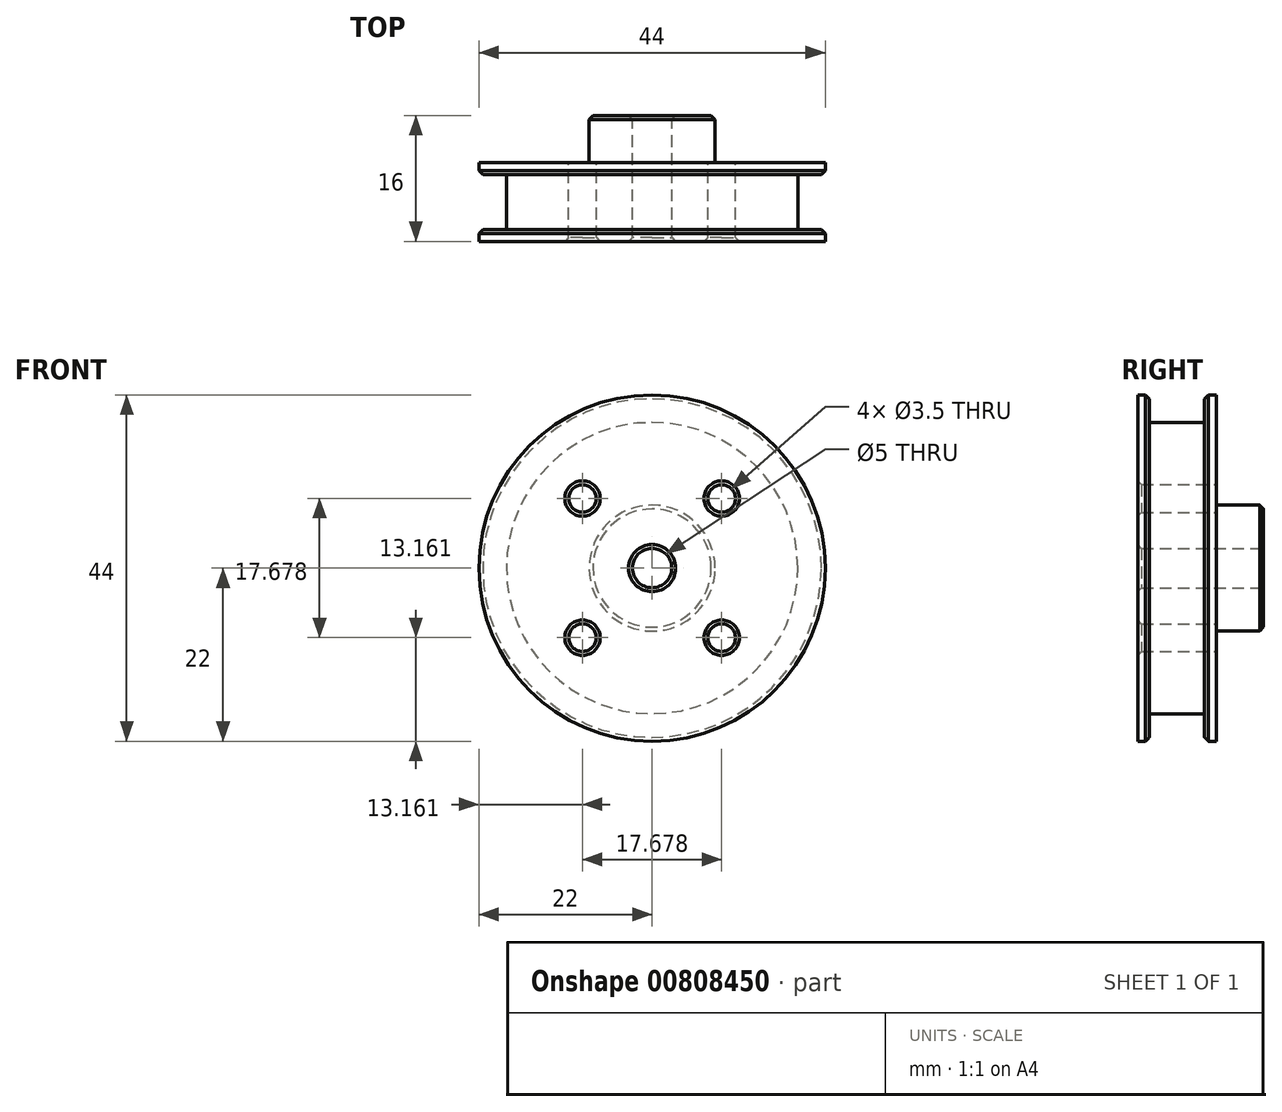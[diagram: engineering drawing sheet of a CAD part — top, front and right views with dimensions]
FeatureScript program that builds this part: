
annotation { "Feature Type Name" : "Feature", "Feature Type Description" : "" }
export const myFeature = defineFeature(function(context is Context, id is Id, definition is map)
    precondition{}
    {
        {
            var Q0;
            Q0=qCreatedBy(makeId("Front.planeOp"),FACE);
            var sketch = newSketch(context, id + "F0", { "sketchPlane" : qUnion([Q0])});
            skCircle(sketch, "E0", {"center": v(0, 0) * mm, "radius": 22 * mm});
            skSolve(sketch);
        }
        {
            var Q0;
            Q0=qSketchRegion(id+"F0",true);
            extrude(context, id + "F1", {"entities" : qUnion([Q0]), "depth" : 10 * mm, "offsetDistance" : 25 * mm, "symmetric" : true});
        }
        {
            var Q0;
            Q0=qCreatedBy(makeId("Front.planeOp"),FACE);
            var sketch = newSketch(context, id + "F2", { "sketchPlane" : qUnion([Q0])});
            skCircle(sketch, "E1", {"center": v(0, 0) * mm, "radius": 18.5 * mm});
            skCircle(sketch, "E2", {"center": v(0, 0) * mm, "radius": 30.43 * mm});
            skSolve(sketch);
        }
        {
            var Q0;
            Q0=qSketchRegion(id+"F2",true);
            extrude(context, id + "F3", {"entities" : qUnion([Q0]), "operationType" : NewBodyOperationType.REMOVE, "depth" : 7 * mm, "offsetDistance" : 25 * mm, "symmetric" : true});
        }
        {
            var Q0;
            Q0=makeQuery(id+"F1.opExtrude","CAP_FACE",FACE,{"disambiguationData":[OSD([sQuery(id+"F0.wireOp",EDGE,"E0")])],"isStart":true});
            var sketch = newSketch(context, id + "F4", { "sketchPlane" : qUnion([Q0])});
            skCircle(sketch, "E3", {"center": v(0, 0) * mm, "radius": 8 * mm});
            skSolve(sketch);
        }
        {
            var Q0;
            Q0=qSketchRegion(id+"F4",true);
            extrude(context, id + "F5", {"entities" : qUnion([Q0]), "operationType" : NewBodyOperationType.ADD, "depth" : 6 * mm, "offsetDistance" : 25 * mm});
        }
        {
            var Q0;
            Q0=makeQuery(id+"F5.opExtrude","CAP_FACE",FACE,{"disambiguationData":[OSD([sQuery(id+"F4.wireOp",EDGE,"E3")])],"isStart":false});
            var sketch = newSketch(context, id + "F6", { "sketchPlane" : qUnion([Q0])});
            skCircle(sketch, "E4", {"center": v(0, 0) * mm, "radius": 2.5 * mm});
            skSolve(sketch);
        }
        {
            var Q0;
            Q0=qSketchRegion(id+"F6",true);
            extrude(context, id + "F7", {"entities" : qUnion([Q0]), "operationType" : NewBodyOperationType.REMOVE, "endBound" : BoundingType.THROUGH_ALL, "oppositeDirection" : true, "depth" : 25 * mm, "offsetDistance" : 25 * mm});
        }
        {
            var Q0;
            Q0=makeQuery(id+"F5.opExtrude","CAP_FACE",FACE,{"disambiguationData":[OSD([sQuery(id+"F4.wireOp",EDGE,"E3")])],"isStart":false});
            var Q1;
            Q1=makeQuery(id+"F5.opExtrude","CAP_EDGE",EDGE,{"disambiguationData":[OSD([sQuery(id+"F4.wireOp",EDGE,"E3")])],"isStart":true});
            var Q2;
            Q2=makeQuery(id+"F3.boolean.opBoolean","INTERSECT",EDGE,{"derivedFrom":[makeQuery(id+"F1.opExtrude","SWEPT_FACE",FACE,{"disambiguationData":[OSD([sQuery(id+"F0.wireOp",EDGE,"E0")])]}),makeQuery(id+"F3.opExtrude","CAP_FACE",FACE,{"disambiguationData":[OSD([sQuery(id+"F2.wireOp",EDGE,"E1"),sQuery(id+"F2.wireOp",EDGE,"E2")])],"isStart":true})]});
            var Q3;
            Q3=makeQuery(id+"F3.boolean.opBoolean","INTERSECT",EDGE,{"derivedFrom":[makeQuery(id+"F1.opExtrude","SWEPT_FACE",FACE,{"disambiguationData":[OSD([sQuery(id+"F0.wireOp",EDGE,"E0")])]}),makeQuery(id+"F3.opExtrude","CAP_FACE",FACE,{"disambiguationData":[OSD([sQuery(id+"F2.wireOp",EDGE,"E1"),sQuery(id+"F2.wireOp",EDGE,"E2")])],"isStart":false})]});
            var Q4;
            Q4=makeQuery(id+"F7.boolean.opBoolean","INTERSECT",EDGE,{"derivedFrom":[makeQuery(id+"F1.opExtrude","CAP_FACE",FACE,{"disambiguationData":[OSD([sQuery(id+"F0.wireOp",EDGE,"E0")])],"isStart":false}),makeQuery(id+"F7.opExtrude","SWEPT_FACE",FACE,{"disambiguationData":[OSD([sQuery(id+"F6.wireOp",EDGE,"E4")])]})]});
            chamfer(context, id + "F8", {"entities" : qUnion([Q0, Q1, Q2, Q3, Q4]), "width" : 0.5 * mm, "tangentPropagation" : true});
        }
        {
            var Q0;
            Q0=makeQuery(id+"F1.opExtrude","CAP_FACE",FACE,{"disambiguationData":[OSD([sQuery(id+"F0.wireOp",EDGE,"E0")])],"isStart":true});
            var sketch = newSketch(context, id + "F9", { "sketchPlane" : qUnion([Q0])});
            skCircle(sketch, "E5", {"center": v(-8.84, 8.84) * mm, "radius": 1.75 * mm});
            skLineSegment(sketch, "E6", {"start": v(-22, 0) * mm, "end": v(0, 0) * mm, "construction": true});
            skLineSegment(sketch, "E7", {"start": v(0, 0) * mm, "end": v(-8.84, 8.84) * mm, "construction": true});
            skCircle(sketch, "E8.1.0", {"center": v(-8.84, -8.84) * mm, "radius": 1.75 * mm});
            skCircle(sketch, "E8.2.0", {"center": v(8.84, -8.84) * mm, "radius": 1.75 * mm});
            skCircle(sketch, "E8.3.0", {"center": v(8.84, 8.84) * mm, "radius": 1.75 * mm});
            skPoint(sketch, "E8.center", {"position": v(0, 0) * mm});
            skSolve(sketch);
        }
        {
            var Q0;
            Q0=qSketchRegion(id+"F9",true);
            extrude(context, id + "F10", {"entities" : qUnion([Q0]), "operationType" : NewBodyOperationType.REMOVE, "endBound" : BoundingType.THROUGH_ALL, "oppositeDirection" : true, "depth" : 25 * mm, "offsetDistance" : 25 * mm});
        }
        {
            var Q0;
            Q0=makeQuery(id+"F10.boolean.opBoolean","INTERSECT",EDGE,{"derivedFrom":[makeQuery(id+"F1.opExtrude","CAP_FACE",FACE,{"disambiguationData":[OSD([sQuery(id+"F0.wireOp",EDGE,"E0")])],"isStart":false}),makeQuery(id+"F10.opExtrude","SWEPT_FACE",FACE,{"disambiguationData":[OSD([sQuery(id+"F9.wireOp",EDGE,"E8.3.0")])]})]});
            var Q1;
            Q1=makeQuery(id+"F10.boolean.opBoolean","INTERSECT",EDGE,{"derivedFrom":[makeQuery(id+"F1.opExtrude","CAP_FACE",FACE,{"disambiguationData":[OSD([sQuery(id+"F0.wireOp",EDGE,"E0")])],"isStart":false}),makeQuery(id+"F10.opExtrude","SWEPT_FACE",FACE,{"disambiguationData":[OSD([sQuery(id+"F9.wireOp",EDGE,"E8.2.0")])]})]});
            var Q2;
            Q2=makeQuery(id+"F10.boolean.opBoolean","INTERSECT",EDGE,{"derivedFrom":[makeQuery(id+"F1.opExtrude","CAP_FACE",FACE,{"disambiguationData":[OSD([sQuery(id+"F0.wireOp",EDGE,"E0")])],"isStart":false}),makeQuery(id+"F10.opExtrude","SWEPT_FACE",FACE,{"disambiguationData":[OSD([sQuery(id+"F9.wireOp",EDGE,"E8.1.0")])]})]});
            var Q3;
            Q3=makeQuery(id+"F10.boolean.opBoolean","INTERSECT",EDGE,{"derivedFrom":[makeQuery(id+"F1.opExtrude","CAP_FACE",FACE,{"disambiguationData":[OSD([sQuery(id+"F0.wireOp",EDGE,"E0")])],"isStart":false}),makeQuery(id+"F10.opExtrude","SWEPT_FACE",FACE,{"disambiguationData":[OSD([sQuery(id+"F9.wireOp",EDGE,"E5")])]})]});
            var Q4;
            Q4=makeQuery(id+"F10.boolean.opBoolean","COPY",EDGE,{"derivedFrom":makeQuery(id+"F10.opExtrude","CAP_EDGE",EDGE,{"disambiguationData":[OSD([sQuery(id+"F9.wireOp",EDGE,"E5")])],"isStart":true})});
            var Q5;
            Q5=makeQuery(id+"F10.boolean.opBoolean","COPY",EDGE,{"derivedFrom":makeQuery(id+"F10.opExtrude","CAP_EDGE",EDGE,{"disambiguationData":[OSD([sQuery(id+"F9.wireOp",EDGE,"E8.3.0")])],"isStart":true})});
            var Q6;
            Q6=makeQuery(id+"F10.boolean.opBoolean","COPY",EDGE,{"derivedFrom":makeQuery(id+"F10.opExtrude","CAP_EDGE",EDGE,{"disambiguationData":[OSD([sQuery(id+"F9.wireOp",EDGE,"E8.2.0")])],"isStart":true})});
            var Q7;
            Q7=makeQuery(id+"F10.boolean.opBoolean","COPY",EDGE,{"derivedFrom":makeQuery(id+"F10.opExtrude","CAP_EDGE",EDGE,{"disambiguationData":[OSD([sQuery(id+"F9.wireOp",EDGE,"E8.1.0")])],"isStart":true})});
            chamfer(context, id + "F11", {"entities" : qUnion([Q0, Q1, Q2, Q3, Q4, Q5, Q6, Q7]), "width" : 0.5 * mm, "tangentPropagation" : true});
        }
    });
